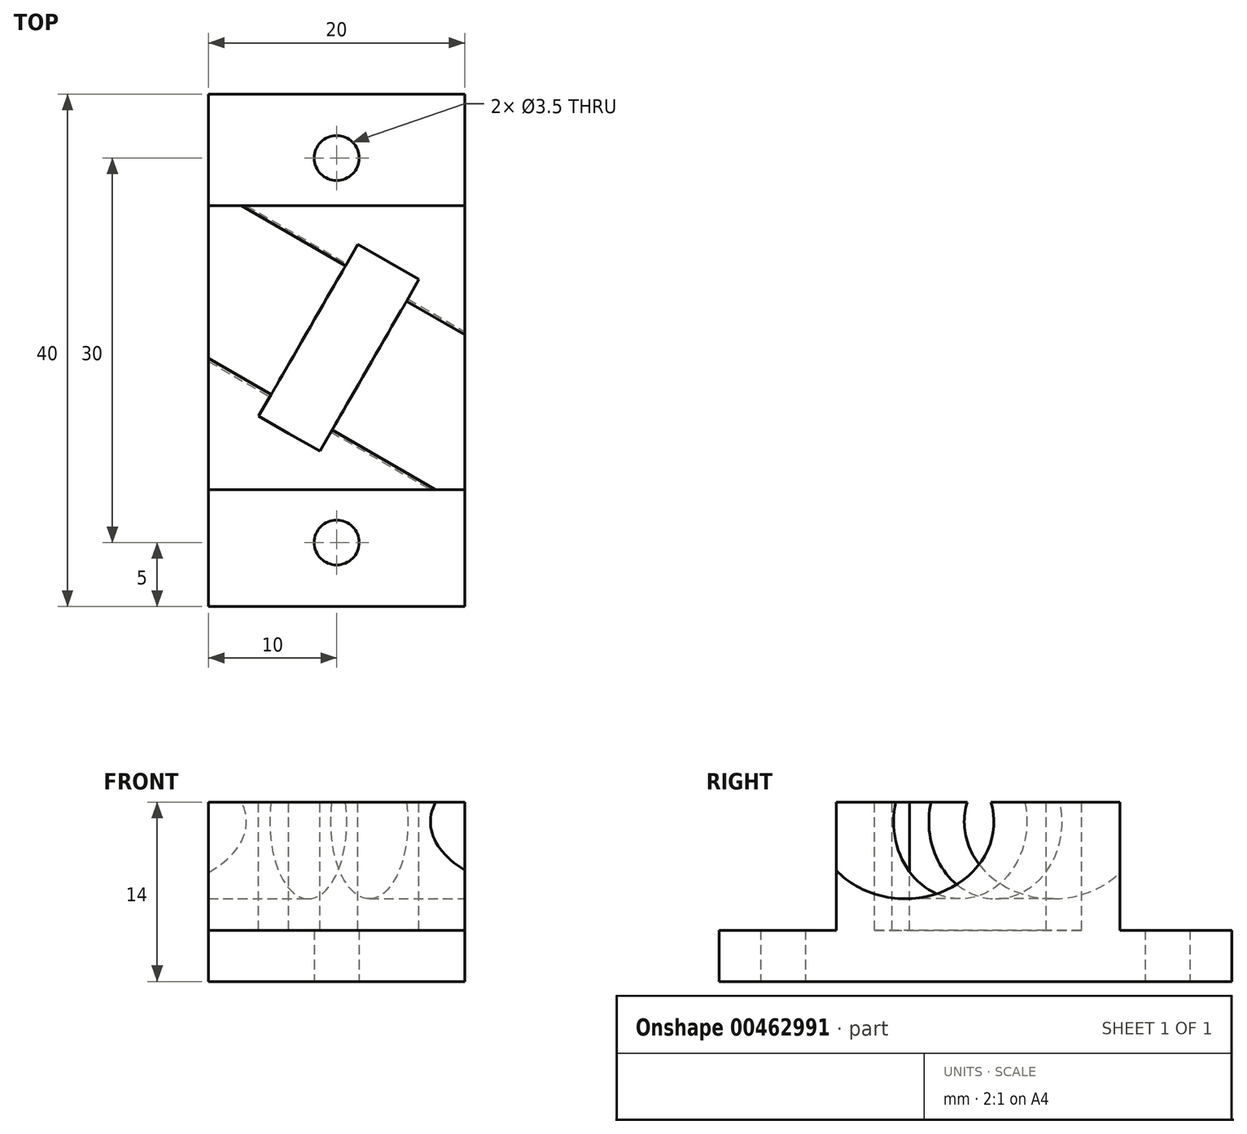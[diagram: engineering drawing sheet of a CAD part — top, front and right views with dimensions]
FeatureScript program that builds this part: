
annotation { "Feature Type Name" : "Feature", "Feature Type Description" : "" }
export const myFeature = defineFeature(function(context is Context, id is Id, definition is map)
    precondition{}
    {
        {
            var Q0;
            Q0=qCreatedBy(makeId("Top.planeOp"),FACE);
            var sketch = newSketch(context, id + "F0", { "sketchPlane" : qUnion([Q0])});
            skLineSegment(sketch, "E0.bottom", {"start": v(10, 20) * mm, "end": v(-10, 20) * mm});
            skLineSegment(sketch, "E0.top", {"start": v(10, -20) * mm, "end": v(-10, -20) * mm});
            skLineSegment(sketch, "E0.left", {"start": v(10, 20) * mm, "end": v(10, -20) * mm});
            skLineSegment(sketch, "E0.right", {"start": v(-10, 20) * mm, "end": v(-10, -20) * mm});
            skPoint(sketch, "E0.middle", {"position": v(0, 0) * mm});
            skLineSegment(sketch, "E1", {"start": v(0, 0) * mm, "end": v(-42.63, 24.61) * mm, "construction": true});
            skLineSegment(sketch, "E2", {"start": v(0, 0) * mm, "end": v(32.05, -18.5) * mm, "construction": true});
            skCircle(sketch, "E3", {"center": v(0, 15) * mm, "radius": 1.75 * mm});
            skCircle(sketch, "E4", {"center": v(0, -15) * mm, "radius": 1.75 * mm});
            skPoint(sketch, "E4.centerSnap0", {"position": v(0, -20) * mm});
            skSolve(sketch);
        }
        {
            var Q0;
            Q0 = qSketchRegion(id + "F0", true);
            extrude(context, id + "F1", {"entities" : qUnion([Q0]), "depth" : 14 * mm, "offsetDistance" : 25 * mm});
        }
        {
            var Q0;
            Q0=makeQuery(id+"F1.opExtrude","CAP_FACE",FACE,{"disambiguationData":[OSD([sQuery(id+"F0.wireOp",EDGE,"E0.bottom"),sQuery(id+"F0.wireOp",EDGE,"E0.top"),sQuery(id+"F0.wireOp",EDGE,"E0.left"),sQuery(id+"F0.wireOp",EDGE,"E0.right"),sQuery(id+"F0.wireOp",EDGE,"E3"),sQuery(id+"F0.wireOp",EDGE,"E4")])],"isStart":false});
            var sketch = newSketch(context, id + "F2", { "sketchPlane" : qUnion([Q0])});
            skLineSegment(sketch, "E5", {"start": v(-20.3, 11.72) * mm, "end": v(0, 0) * mm, "construction": true});
            skLineSegment(sketch, "E6", {"start": v(0, 0) * mm, "end": v(20.14, -11.63) * mm, "construction": true});
            skLineSegment(sketch, "E7", {"start": v(-3.75, -6.5) * mm, "end": v(-6.09, -5.15) * mm});
            skLineSegment(sketch, "E8", {"start": v(-6.09, -5.15) * mm, "end": v(1.66, 8.28) * mm});
            skLineSegment(sketch, "E9", {"start": v(1.66, 8.28) * mm, "end": v(6.42, 5.53) * mm});
            skLineSegment(sketch, "E10", {"start": v(6.42, 5.53) * mm, "end": v(-1.3, -7.87) * mm});
            skLineSegment(sketch, "E11", {"start": v(-1.3, -7.87) * mm, "end": v(-3.75, -6.5) * mm});
            skLineSegment(sketch, "E12", {"start": v(10, 11.28) * mm, "end": v(10, 20) * mm});
            skLineSegment(sketch, "E13", {"start": v(10, 20) * mm, "end": v(-10, 20) * mm});
            skLineSegment(sketch, "E14", {"start": v(-10, 20) * mm, "end": v(-10, 11.28) * mm});
            skLineSegment(sketch, "E15", {"start": v(-10, 11.28) * mm, "end": v(10, 11.28) * mm});
            skLineSegment(sketch, "E16.bottom", {"start": v(10, -20) * mm, "end": v(-10, -20) * mm});
            skLineSegment(sketch, "E16.top", {"start": v(10, -10.87) * mm, "end": v(-10, -10.87) * mm});
            skLineSegment(sketch, "E16.left", {"start": v(10, -20) * mm, "end": v(10, -10.87) * mm});
            skLineSegment(sketch, "E16.right", {"start": v(-10, -20) * mm, "end": v(-10, -10.87) * mm});
            skSolve(sketch);
        }
        {
            var Q0;
            Q0 = qSketchRegion(id + "F2", true);
            extrude(context, id + "F3", {"entities" : qUnion([Q0]), "operationType" : NewBodyOperationType.REMOVE, "oppositeDirection" : true, "depth" : 10 * mm, "offsetDistance" : 25 * mm});
        }
        {
            var Q0;
            Q0=makeQuery(id+"F3.boolean.opBoolean","COPY",FACE,{"derivedFrom":makeQuery(id+"F3.opExtrude","SWEPT_FACE",FACE,{"disambiguationData":[OSD([sQuery(id+"F2.wireOp",EDGE,"E8")])]})});
            var sketch = newSketch(context, id + "F4", { "sketchPlane" : qUnion([Q0])});
            skCircle(sketch, "E17", {"center": v(0.25, 12.45) * mm, "radius": 6 * mm});
            skPoint(sketch, "E17.centerSnap0", {"position": v(0.25, 14) * mm});
            skSolve(sketch);
        }
        {
            var Q0;
            Q0 = qSketchRegion(id + "F4", true);
            extrude(context, id + "F5", {"entities" : qUnion([Q0]), "operationType" : NewBodyOperationType.REMOVE, "oppositeDirection" : true, "depth" : 14 * mm, "offsetDistance" : 25 * mm, "hasSecondDirection" : true, "secondDirectionOppositeDirection" : false, "secondDirectionDepth" : 20 * mm});
        }
    });
